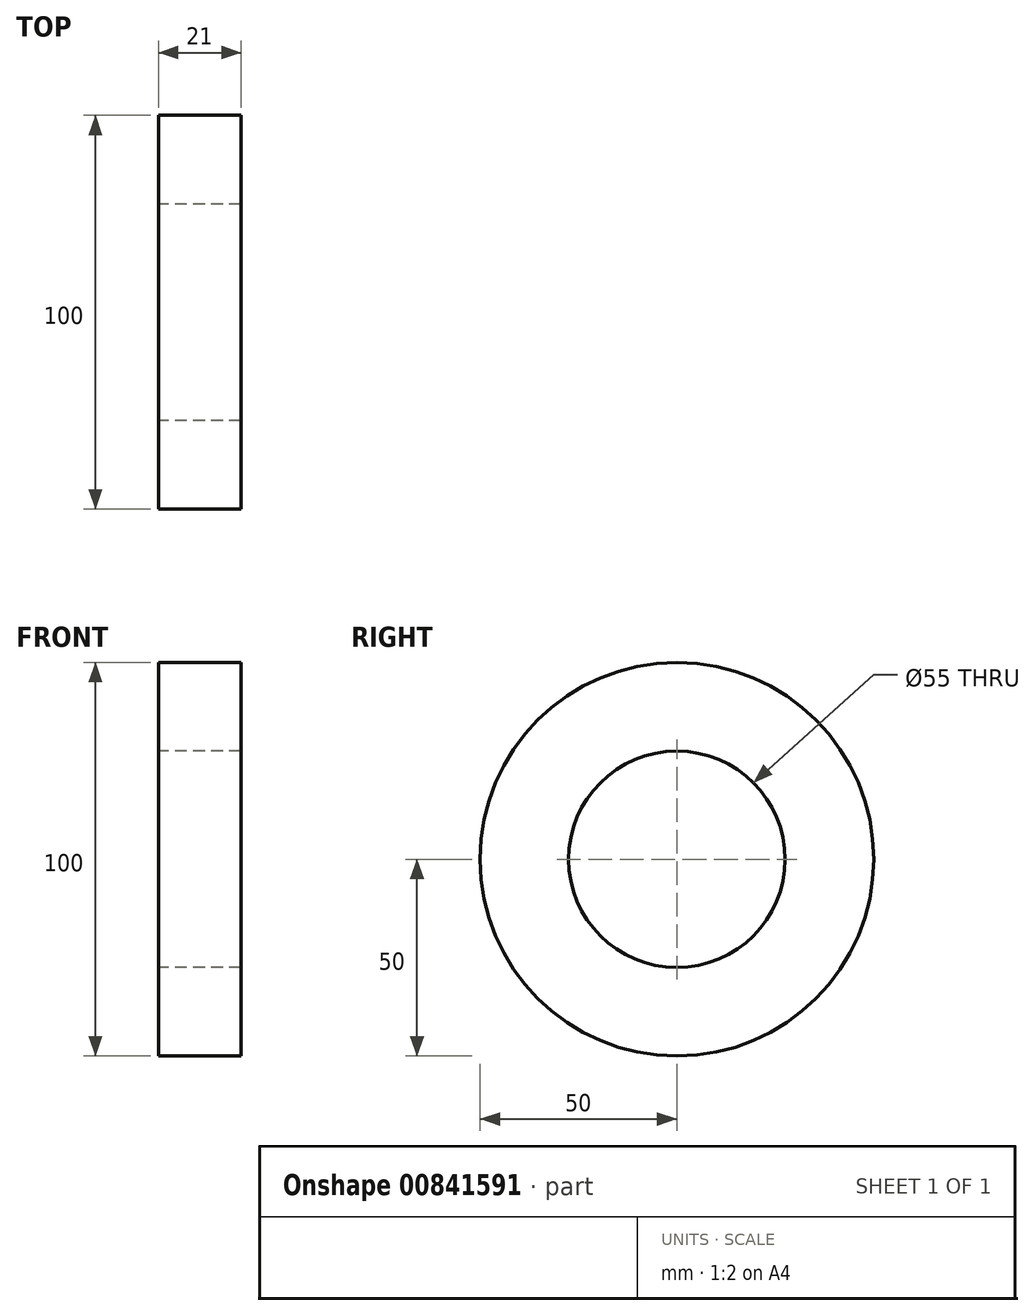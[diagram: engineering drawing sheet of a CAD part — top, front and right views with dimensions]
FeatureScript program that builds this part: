
annotation { "Feature Type Name" : "Feature", "Feature Type Description" : "" }
export const myFeature = defineFeature(function(context is Context, id is Id, definition is map)
    precondition{}
    {
        {
            var Q0;
            Q0=qCreatedBy(makeId("Front.planeOp"),FACE);
            var sketch = newSketch(context, id + "F0", { "sketchPlane" : qUnion([Q0])});
            skLineSegment(sketch, "E0.bottom", {"start": v(0, 27.5) * mm, "end": v(21, 27.5) * mm});
            skLineSegment(sketch, "E0.top", {"start": v(0, 50) * mm, "end": v(21, 50) * mm});
            skLineSegment(sketch, "E0.left", {"start": v(0, 27.5) * mm, "end": v(0, 50) * mm});
            skLineSegment(sketch, "E0.right", {"start": v(21, 27.5) * mm, "end": v(21, 50) * mm});
            skLineSegment(sketch, "E1", {"start": v(0, 0) * mm, "end": v(29.27, 0) * mm, "construction": true});
            skSolve(sketch);
        }
        {
            var Q0;
            Q0 = qSketchRegion(id + "F0", true);
            var Q1;
            Q1=sQuery(id+"F0.wireOp",EDGE,"E1");
            revolve(context, id + "F1", {"surfaceOperationType" : NewSurfaceOperationType.NEW, "entities" : qUnion([Q0]), "axis" : qUnion([Q1]), "revolveType" : RevolveType.FULL});
        }
    });
